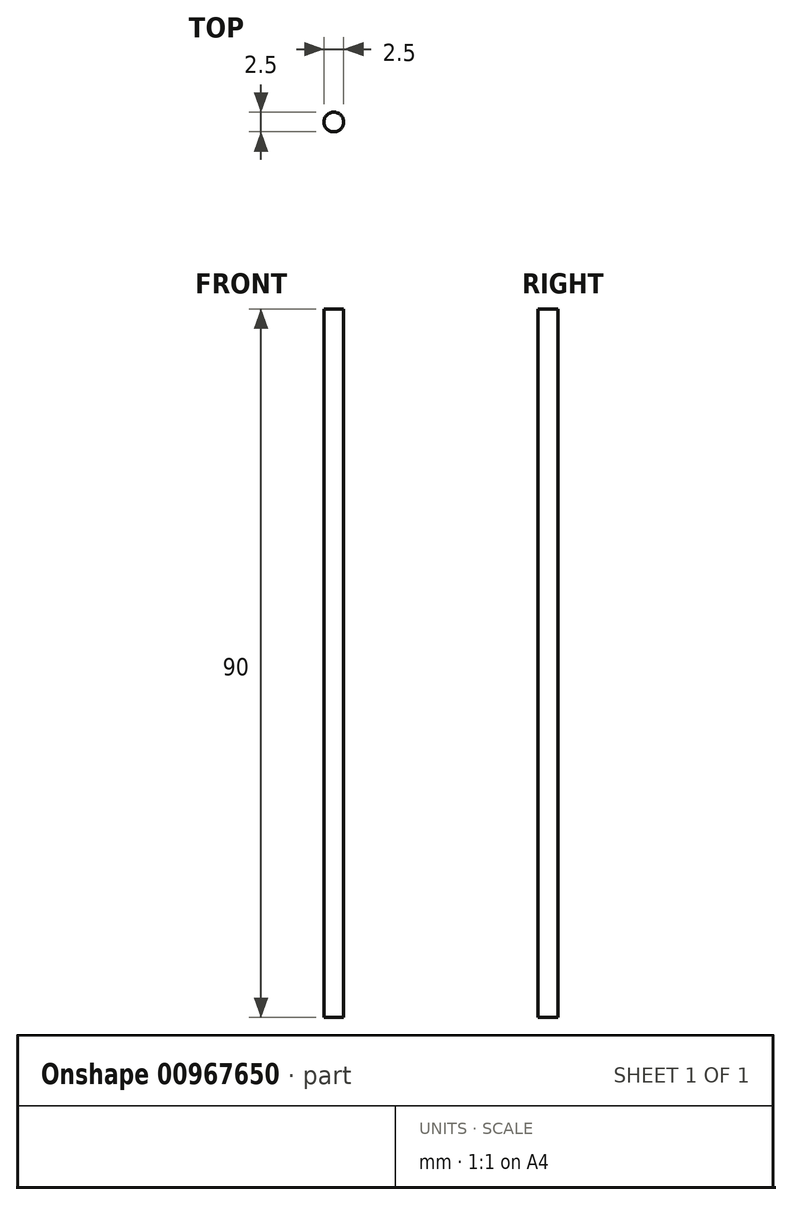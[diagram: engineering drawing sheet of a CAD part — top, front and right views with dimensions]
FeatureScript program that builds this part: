
annotation { "Feature Type Name" : "Feature", "Feature Type Description" : "" }
export const myFeature = defineFeature(function(context is Context, id is Id, definition is map)
    precondition{}
    {
        {
            var Q0;
            Q0=qCreatedBy(makeId("Top.planeOp"),FACE);
            var sketch = newSketch(context, id + "F0", { "sketchPlane" : qUnion([Q0])});
            skCircle(sketch, "E0", {"center": v(0, 0) * mm, "radius": 1.25 * mm});
            skSolve(sketch);
        }
        {
            var Q0;
            Q0 = qSketchRegion(id + "F0", true);
            extrude(context, id + "F1", {"entities" : qUnion([Q0]), "depth" : 90 * mm, "offsetDistance" : 25.4 * mm});
        }
    });
